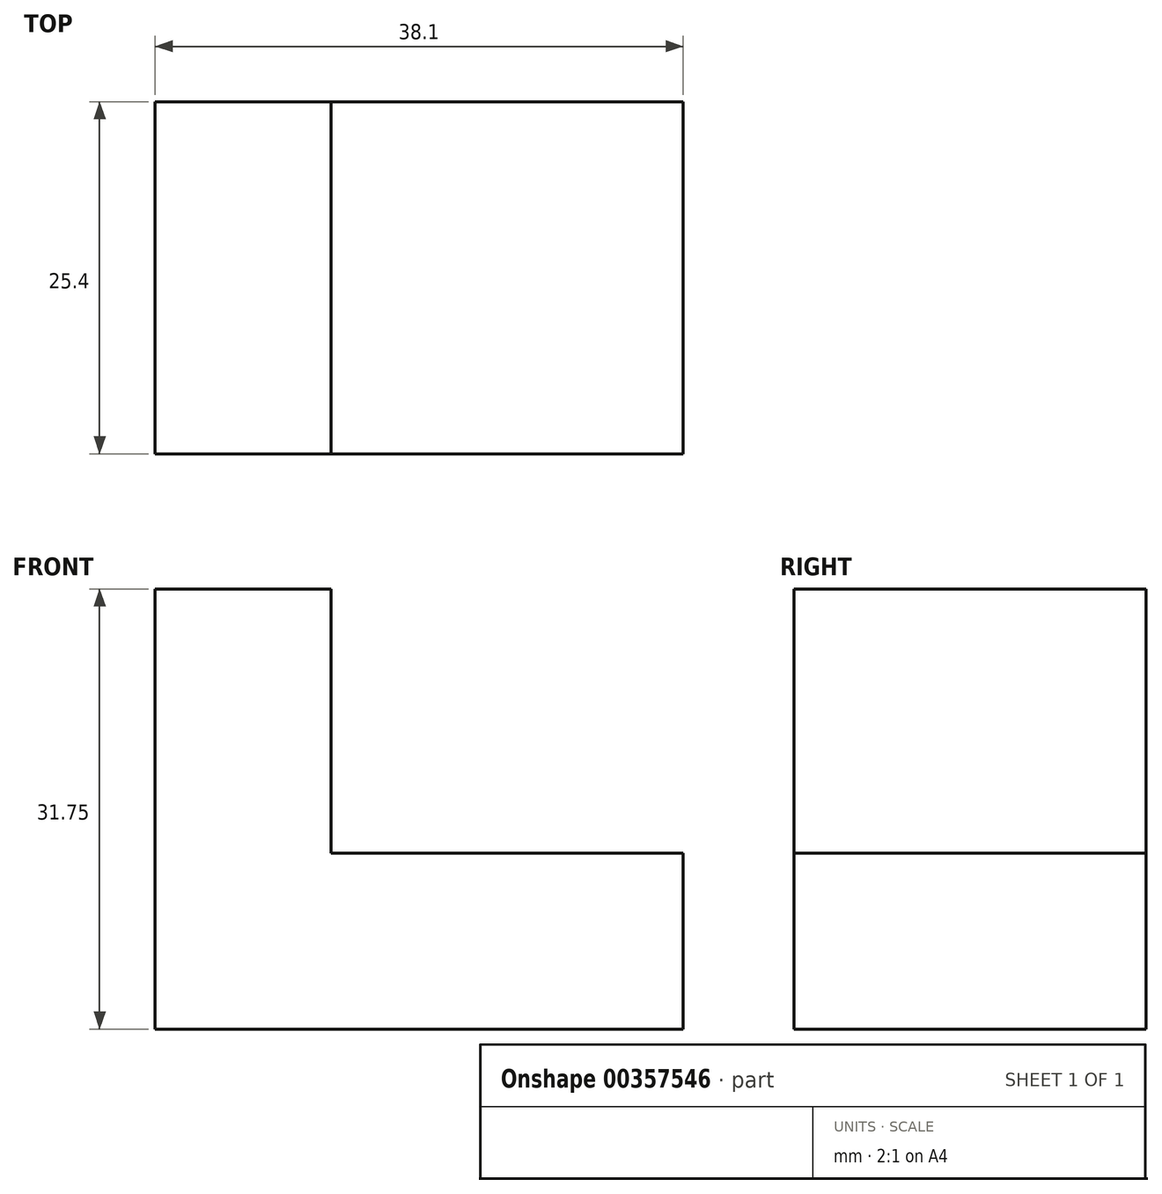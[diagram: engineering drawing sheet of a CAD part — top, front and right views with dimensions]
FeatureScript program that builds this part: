
annotation { "Feature Type Name" : "Feature", "Feature Type Description" : "" }
export const myFeature = defineFeature(function(context is Context, id is Id, definition is map)
    precondition{}
    {
        {
            var Q0;
            Q0=qCreatedBy(makeId("Front.planeOp"),FACE);
            var sketch = newSketch(context, id + "F0", { "sketchPlane" : qUnion([Q0])});
            skLineSegment(sketch, "E0", {"start": v(-53.2, 31.75) * mm, "end": v(-40.5, 31.75) * mm});
            skLineSegment(sketch, "E1", {"start": v(-40.5, 31.75) * mm, "end": v(-40.5, 12.7) * mm});
            skLineSegment(sketch, "E2", {"start": v(-15.1, 12.7) * mm, "end": v(-15.1, 0) * mm});
            skLineSegment(sketch, "E3", {"start": v(-15.1, 0) * mm, "end": v(-53.2, 0) * mm});
            skLineSegment(sketch, "E4", {"start": v(-40.5, 12.7) * mm, "end": v(-15.1, 12.7) * mm});
            skLineSegment(sketch, "E5", {"start": v(-53.2, 31.75) * mm, "end": v(-53.2, 0) * mm});
            skSolve(sketch);
        }
        {
            var Q0;
            Q0 = qSketchRegion(id + "F0", true);
            extrude(context, id + "F1", {"entities" : qUnion([Q0]), "depth" : 25.4 * mm});
        }
    });
